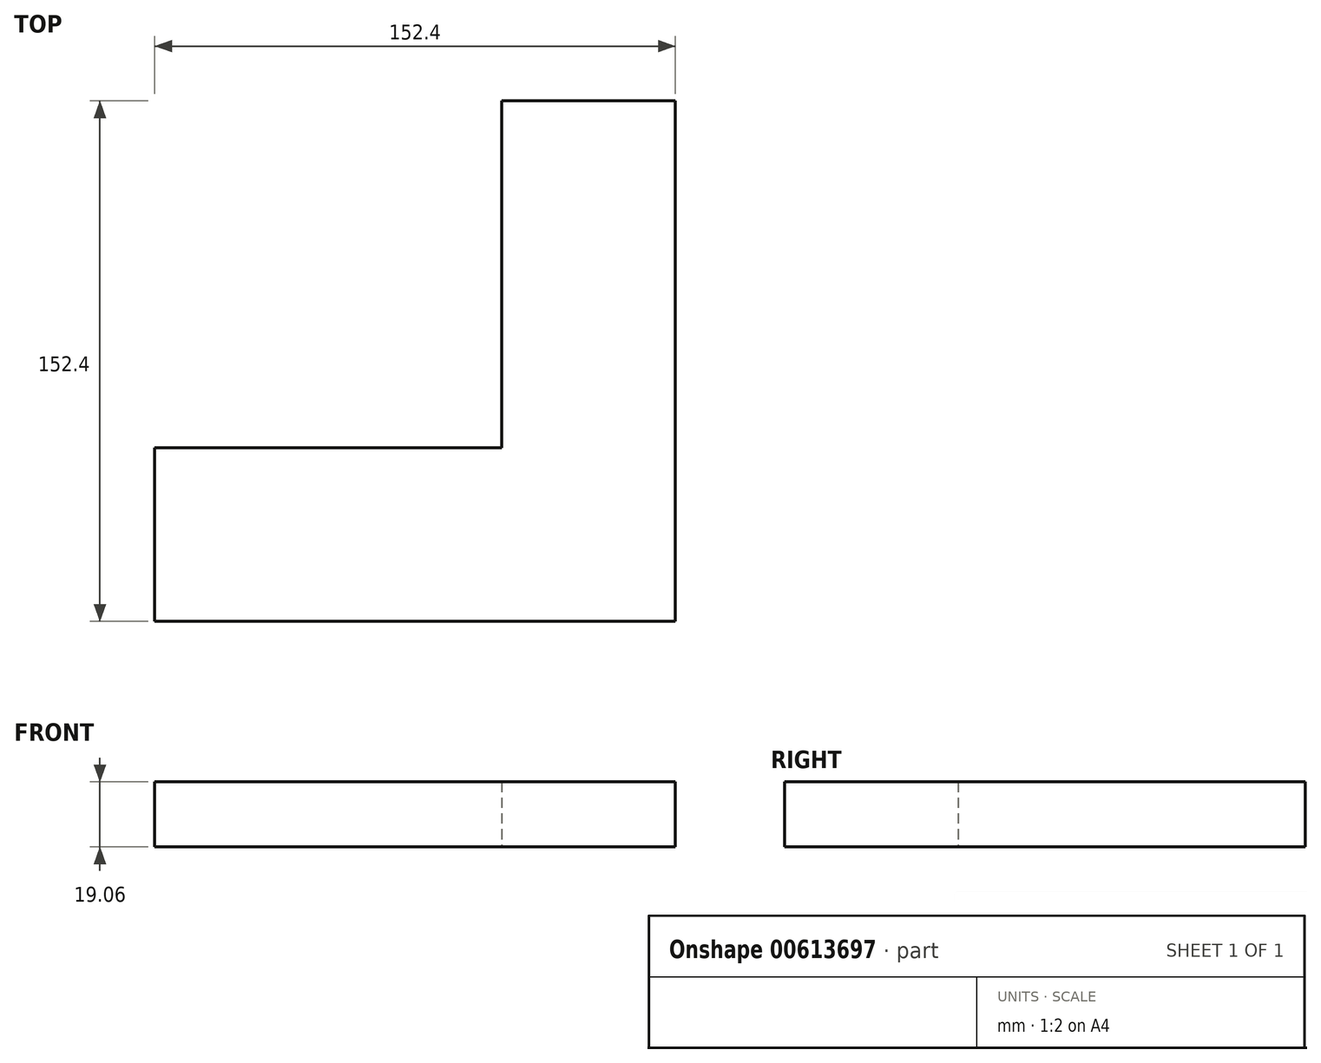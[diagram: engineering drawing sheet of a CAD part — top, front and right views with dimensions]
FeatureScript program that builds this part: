
annotation { "Feature Type Name" : "Feature", "Feature Type Description" : "" }
export const myFeature = defineFeature(function(context is Context, id is Id, definition is map)
    precondition{}
    {
        {
            var Q0;
            Q0=qCreatedBy(makeId("Top.planeOp"),FACE);
            var sketch = newSketch(context, id + "F0", { "sketchPlane" : qUnion([Q0])});
            skLineSegment(sketch, "E0.bottom", {"start": v(0, 0) * mm, "end": v(-152.4, 0) * mm});
            skLineSegment(sketch, "E0.top", {"start": v(0, 50.8) * mm, "end": v(-152.4, 50.8) * mm});
            skLineSegment(sketch, "E0.left", {"start": v(0, 0) * mm, "end": v(0, 50.8) * mm});
            skLineSegment(sketch, "E0.right", {"start": v(-152.4, 0) * mm, "end": v(-152.4, 50.8) * mm});
            skLineSegment(sketch, "E1.bottom", {"start": v(0, 0) * mm, "end": v(-50.8, 0) * mm});
            skLineSegment(sketch, "E1.top", {"start": v(0, 152.4) * mm, "end": v(-50.8, 152.4) * mm});
            skLineSegment(sketch, "E1.left", {"start": v(0, 0) * mm, "end": v(0, 152.4) * mm});
            skLineSegment(sketch, "E1.right", {"start": v(-50.8, 0) * mm, "end": v(-50.8, 152.4) * mm});
            skSolve(sketch);
        }
        {
            var Q0;
            {var subQ0=sQuery(id+"F0.wireOp",EDGE,"E0.bottom");Q0=makeQuery(id+"F0.imprint","IMPRINT",FACE,{"disambiguationData":[TD([[makeQuery(id+"F0.imprint","IMPRINT",EDGE,{"derivedFrom":subQ0}),-1.0]])]});}
            extrude(context, id + "F1", {"entities" : qUnion([Q0]), "depth" : 9.52 * mm, "offsetDistance" : 25.4 * mm});
        }
        {
            var Q0;
            {var subQ5=sQuery(id+"F0.wireOp",EDGE,"E1.bottom");Q0=makeQuery(id+"F0.imprint","IMPRINT",FACE,{"disambiguationData":[TD([[makeQuery(id+"F0.imprint","IMPRINT",EDGE,{"derivedFrom":subQ5}),-1.0]])]});}
            var Q1;
            {var subQ0=sQuery(id+"F0.wireOp",EDGE,"E0.bottom");Q1=makeQuery(id+"F0.imprint","IMPRINT",FACE,{"disambiguationData":[TD([[makeQuery(id+"F0.imprint","IMPRINT",EDGE,{"derivedFrom":subQ0}),-1.0]])]});}
            extrude(context, id + "F2", {"entities" : qUnion([Q0, Q1]), "operationType" : NewBodyOperationType.ADD, "oppositeDirection" : true, "depth" : 9.52 * mm, "offsetDistance" : 25.4 * mm});
        }
        {
            var Q0;
            {var subQ5=sQuery(id+"F0.wireOp",EDGE,"E1.bottom");Q0=makeQuery(id+"F0.imprint","IMPRINT",FACE,{"disambiguationData":[TD([[makeQuery(id+"F0.imprint","IMPRINT",EDGE,{"derivedFrom":subQ5}),-1.0]])]});}
            var Q1;
            {var subQ5=sQuery(id+"F0.wireOp",EDGE,"E1.top");Q1=makeQuery(id+"F0.imprint","IMPRINT",FACE,{"disambiguationData":[TD([[makeQuery(id+"F0.imprint","IMPRINT",EDGE,{"derivedFrom":subQ5}),1.0]])]});}
            extrude(context, id + "F3", {"entities" : qUnion([Q0, Q1]), "depth" : 9.52 * mm, "offsetDistance" : 25.4 * mm});
        }
        {
            var Q0;
            {var subQ5=sQuery(id+"F0.wireOp",EDGE,"E1.top");Q0=makeQuery(id+"F0.imprint","IMPRINT",FACE,{"disambiguationData":[TD([[makeQuery(id+"F0.imprint","IMPRINT",EDGE,{"derivedFrom":subQ5}),1.0]])]});}
            extrude(context, id + "F4", {"entities" : qUnion([Q0]), "operationType" : NewBodyOperationType.ADD, "oppositeDirection" : true, "depth" : 9.52 * mm, "offsetDistance" : 25.4 * mm});
        }
    });
